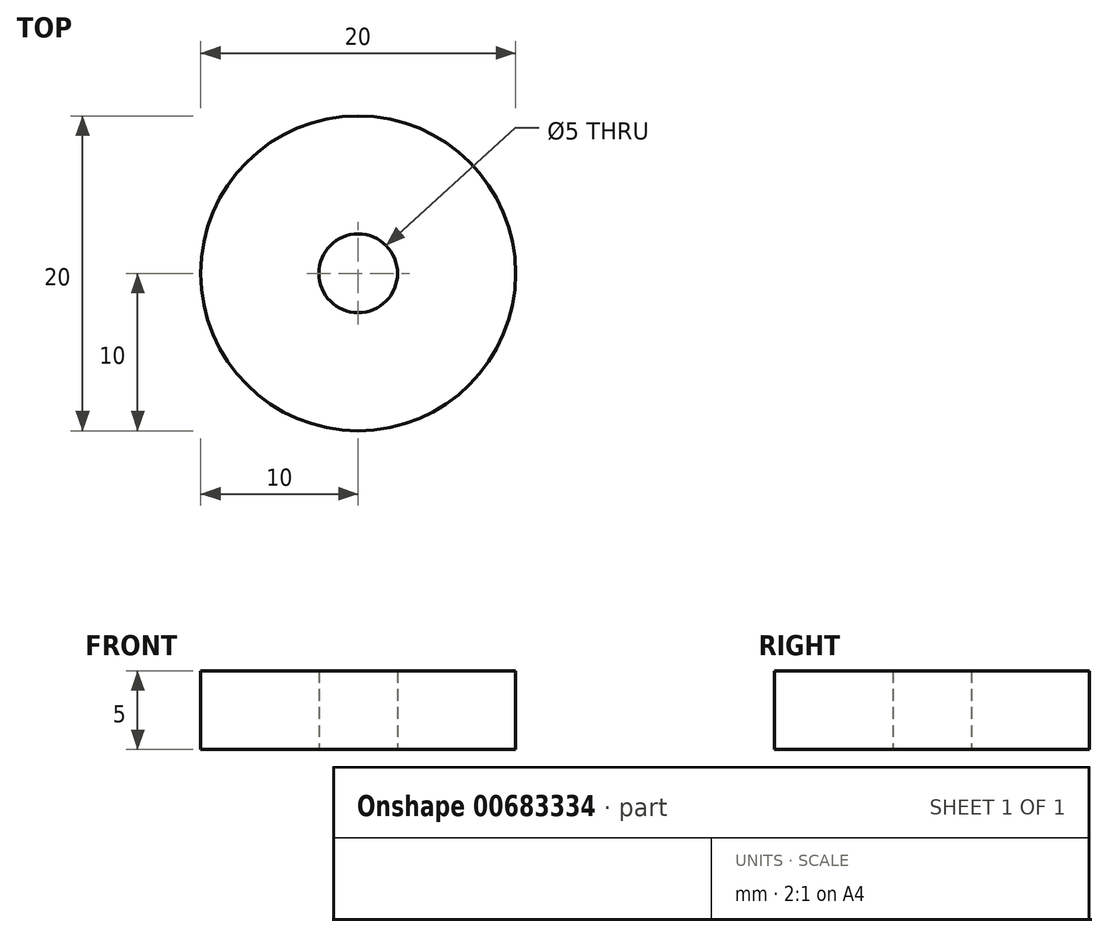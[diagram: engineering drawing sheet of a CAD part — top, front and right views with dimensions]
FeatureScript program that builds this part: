
annotation { "Feature Type Name" : "Feature", "Feature Type Description" : "" }
export const myFeature = defineFeature(function(context is Context, id is Id, definition is map)
    precondition{}
    {
        {
            var Q0;
            Q0=qCreatedBy(makeId("Top.planeOp"),FACE);
            var sketch = newSketch(context, id + "F0", { "sketchPlane" : qUnion([Q0])});
            skCircle(sketch, "E0", {"center": v(0, 0) * mm, "radius": 10 * mm});
            skCircle(sketch, "E1", {"center": v(0, 0) * mm, "radius": 2.5 * mm});
            skSolve(sketch);
        }
        {
            var Q0;
            Q0 = qSketchRegion(id + "F0", true);
            extrude(context, id + "F1", {"entities" : qUnion([Q0]), "depth" : 5 * mm, "offsetDistance" : 25 * mm});
        }
    });
